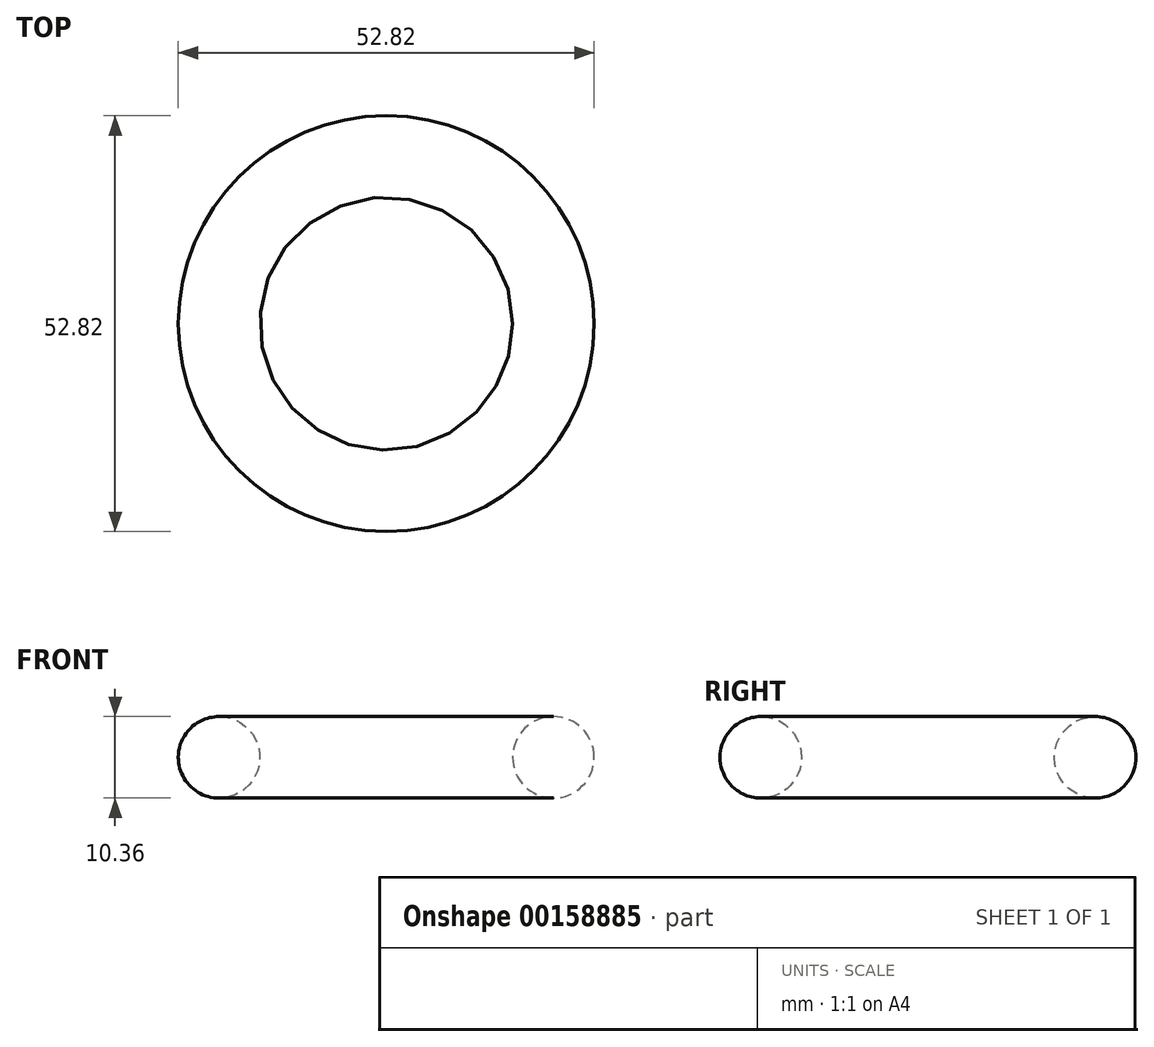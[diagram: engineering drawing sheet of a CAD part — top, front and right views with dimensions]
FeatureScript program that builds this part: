
annotation { "Feature Type Name" : "Feature", "Feature Type Description" : "" }
export const myFeature = defineFeature(function(context is Context, id is Id, definition is map)
    precondition{}
    {
        {
            var Q0;
            Q0=qCreatedBy(makeId("Front.planeOp"),FACE);
            var sketch = newSketch(context, id + "F0", { "sketchPlane" : qUnion([Q0])});
            skCircle(sketch, "E0", {"center": v(-21.23, 0) * mm, "radius": 5.18 * mm});
            skLineSegment(sketch, "E1", {"start": v(0, 62.62) * mm, "end": v(0, -65.63) * mm, "construction": true});
            skSolve(sketch);
        }
        {
            var Q0;
            Q0=makeQuery(id+"F0.imprint","IMPRINT",FACE,{"disambiguationData":[TD([[makeQuery(id+"F0.imprint","IMPRINT",EDGE,{"derivedFrom":sQuery(id+"F0.wireOp",EDGE,"E0")}),1.0]])]});
            var Q1;
            Q1=sQuery(id+"F0.wireOp",EDGE,"E1");
            revolve(context, id + "F1", {"surfaceOperationType" : NewSurfaceOperationType.NEW, "entities" : qUnion([Q0]), "axis" : qUnion([Q1]), "revolveType" : RevolveType.FULL});
        }
    });
